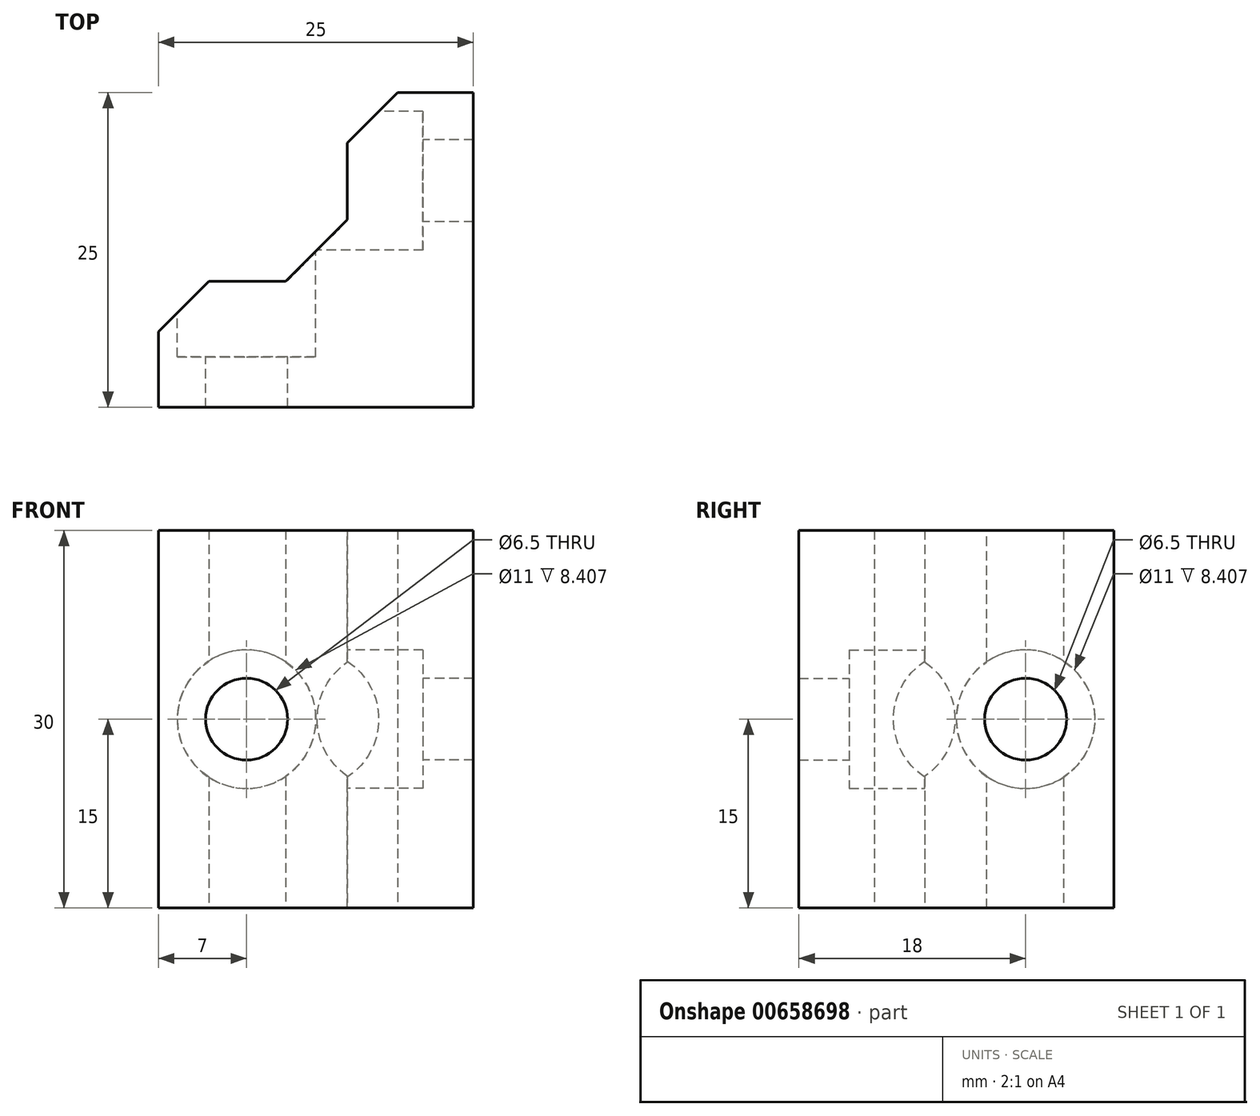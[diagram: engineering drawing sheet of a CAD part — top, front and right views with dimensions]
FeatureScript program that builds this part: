
annotation { "Feature Type Name" : "Feature", "Feature Type Description" : "" }
export const myFeature = defineFeature(function(context is Context, id is Id, definition is map)
    precondition{}
    {
        {
            var Q0;
            Q0=qCreatedBy(makeId("Top.planeOp"),FACE);
            var sketch = newSketch(context, id + "F0", { "sketchPlane" : qUnion([Q0])});
            skLineSegment(sketch, "E0", {"start": v(0, 0) * mm, "end": v(-25, 0) * mm});
            skLineSegment(sketch, "E1", {"start": v(-25, 0) * mm, "end": v(-25, 6) * mm});
            skLineSegment(sketch, "E2", {"start": v(-25, 6) * mm, "end": v(-25, 6) * mm});
            skLineSegment(sketch, "E3", {"start": v(-25, 6) * mm, "end": v(-6, 25) * mm});
            skLineSegment(sketch, "E4", {"start": v(-6, 25) * mm, "end": v(-6, 25) * mm});
            skLineSegment(sketch, "E5", {"start": v(-6, 25) * mm, "end": v(0, 25) * mm});
            skLineSegment(sketch, "E6", {"start": v(0, 25) * mm, "end": v(0, 0) * mm});
            skLineSegment(sketch, "E7.rect.bottom", {"start": v(-10, 21) * mm, "end": v(-21, 21) * mm});
            skLineSegment(sketch, "E7.rect.top", {"start": v(-10, 10) * mm, "end": v(-21, 10) * mm});
            skLineSegment(sketch, "E7.rect.left", {"start": v(-10, 21) * mm, "end": v(-10, 10) * mm});
            skLineSegment(sketch, "E7.rect.right", {"start": v(-21, 21) * mm, "end": v(-21, 10) * mm});
            skPoint(sketch, "E7.rect.middle", {"position": v(-15.5, 15.5) * mm});
            skSolve(sketch);
        }
        {
            var Q0;
            Q0=makeQuery(id+"F0.imprint","IMPRINT",FACE,{"disambiguationData":[TD([[makeQuery(id+"F0.imprint","IMPRINT",EDGE,{"derivedFrom":sQuery(id+"F0.wireOp",EDGE,"E0")}),-1.0]])]});
            extrude(context, id + "F1", {"entities" : qUnion([Q0]), "depth" : 30 * mm});
        }
        {
            var Q0;
            Q0=makeQuery(id+"F1.opExtrude","SWEPT_FACE",FACE,{"disambiguationData":[OSD([sQuery(id+"F0.wireOp",EDGE,"E7.rect.left")])]});
            var sketch = newSketch(context, id + "F2", { "sketchPlane" : qUnion([Q0])});
            skPoint(sketch, "E8", {"position": v(-18, 15) * mm});
            skPoint(sketch, "E8.positionSnap0", {"position": v(-21, 15) * mm});
            skSolve(sketch);
        }
        {
            var Q0;
            Q0=sQuery(id+"F2.wireOp",VERTEX,"E8");
            var Q1;
            Q1=makeQuery(id+"F1.opExtrude","SWEPT_BODY",BODY,{"disambiguationData":[OSD([sQuery(id+"F0.wireOp",EDGE,"E0"),sQuery(id+"F0.wireOp",EDGE,"E1"),sQuery(id+"F0.wireOp",EDGE,"E3"),sQuery(id+"F0.wireOp",EDGE,"E5"),sQuery(id+"F0.wireOp",EDGE,"E6"),sQuery(id+"F0.wireOp",EDGE,"E7.rect.top"),sQuery(id+"F0.wireOp",EDGE,"E7.rect.left")])]});
            hole(context, id + "F3", {"style" : HoleStyle.C_BORE, "holeDiameter" : 6.5 * mm, "cBoreDiameter" : 11 * mm, "cBoreDepth" : 3.5 * mm, "endStyle" : HoleEndStyle.THROUGH, "locations" : qUnion([Q0]), "scope" : qUnion([Q1])});
        }
        {
            var Q0;
            Q0=makeQuery(id+"F1.opExtrude","SWEPT_FACE",FACE,{"disambiguationData":[OSD([sQuery(id+"F0.wireOp",EDGE,"E7.rect.top")])]});
            var sketch = newSketch(context, id + "F4", { "sketchPlane" : qUnion([Q0])});
            skPoint(sketch, "E9", {"position": v(18, 15) * mm});
            skPoint(sketch, "E9.positionSnap0", {"position": v(21, 15) * mm});
            skSolve(sketch);
        }
        {
            var Q0;
            Q0=sQuery(id+"F4.wireOp",VERTEX,"E9");
            var Q1;
            Q1=makeQuery(id+"F1.opExtrude","SWEPT_BODY",BODY,{"disambiguationData":[OSD([sQuery(id+"F0.wireOp",EDGE,"E0"),sQuery(id+"F0.wireOp",EDGE,"E1"),sQuery(id+"F0.wireOp",EDGE,"E3"),sQuery(id+"F0.wireOp",EDGE,"E5"),sQuery(id+"F0.wireOp",EDGE,"E6"),sQuery(id+"F0.wireOp",EDGE,"E7.rect.top"),sQuery(id+"F0.wireOp",EDGE,"E7.rect.left")])]});
            hole(context, id + "F5", {"style" : HoleStyle.C_BORE, "holeDiameter" : 6.5 * mm, "cBoreDiameter" : 11 * mm, "cBoreDepth" : 3.5 * mm, "endStyle" : HoleEndStyle.THROUGH, "locations" : qUnion([Q0]), "scope" : qUnion([Q1])});
        }
        {
            var Q0;
            Q0=makeQuery(id+"F1.opExtrude","SWEPT_EDGE",EDGE,{"disambiguationData":[OSD([sQuery(id+"F0.wireOp",EDGE,"E7.rect.top"),sQuery(id+"F0.wireOp",EDGE,"E7.rect.left")])]});
            chamfer(context, id + "F6", {"entities" : qUnion([Q0]), "width" : 4.9 * mm, "tangentPropagation" : true});
        }
    });
